# Revit family: Lighting_Pendants_Focus_Yoyo_Pendant
name_source: partatom
category: Lighting Fixtures
revit_build: Autodesk Revit 2017 (Build: 20190508_0315(x64)
units: mm (PartAtom-declared; Revit-internal decimal feet)

## family parameters
Always vertical = Yes
Cut with Voids When Loaded = No
Host = Ceiling
Light Source = Yes
OmniClass Number = 23.80.70.00
OmniClass Title = Lighting
Part Type = Normal
Room Calculation Point = No
Round Connector Dimension = Use Diameter
Shared = No

## types (1)
- Yoyo - Pendant
    AssetType = Fixed
    BIMObjectName = Lighting_Pendants_Focus_Yoyo_Pendant
    Brand = Focus Lighting
    Category = Indoor luminaires
    Color = Various
    Color Filter = 16777215
    Constituents = 3m white cable
    ConvergoRefNr = 0147-2006-0004-DK
    DefaultElevation = 0 mm  [stored 0 ft]
    Description = Yoyo is a new range of elegant indoor fixtures. The Yoyo luminaires are edge lit and are completely free of markings of internal components.
    Design = C.F. Møller Architects
    Dimming Lamp Color Temperature Shift = <None>
    DurationUnit = Hours
    ElectricalDeviceNominalPower = 0
    Emit Shape Visible in Rendering = No
    Emit from Circle Diameter = 610 mm
    ExpectedLife = 50000
    Features = LED: Edge lit; Top reflector + Light guide plate (LGP)
    Finish = Raw or painted aluminium
    HasProtectiveEarth = No
    IP_Code = IP20
    IfcExportAs = IfcLightFixtureType
    IfcExportType = NOTDEFINED
    InsulationStandardClass = Class 1
    LensMaterial = Acrylic, Clear
    LightFixtureMountingType = Suspended
    LightFixturePlacingType = Surface
    LightFixtureSecondaryMaterial = Plastic, Opaque White
    MaintenanceFactor = 0
    ManufacturerName = Focus Lighting
    ManufacturerURL = http://focus-lighting.dk
    Material = Aluminium
    NBSDescription = General purpose luminaires
    NBSReference = 90-60-50/405
    Name = Focus_Yoyo_Pendant
    NominalCurrent = 0 A
    NominalDiameter = 535 mm
    NominalFrequencyRange = 50 Hz
    NominalLength = 535 mm
    NominalRadius = 268 mm
    NominalVoltage = 220 V
    NominalVoltageCalc = 0 V
    NominalWidth = 535 mm
    NumberOfPoles = 1
    NumberOfSources = 0
    PhaseAngle = 0.00°
    Photometric Web File = YOYO 350 500mA 16W 3000K CRI90 CDP Prismatisk.IES
    ProductInformation = Yoyo is a new range of elegant indoor fixtures. The Yoyo luminaires are edge lit and are completely free of markings of internal components.
    Shape = Sculptured
    Size = 535x535x77 mm
    Tilt Angle = 90.00°
    TotalWattage = 26 W
    URL = https://focus-lighting.clients.ubivox.com
    Uniclass2 = Pr_70_70_49_86
    Uniclass2015Description = Pendant luminaires
    Uniclass2015Reference = Pr_70_70_48_62
    UsageCurrent = 0 A
    Version = 1
    VersionDate = 18/06/2020
    WarrantyDurationUnit = Hours
    Weight = 4.2 kg

note: [stored X ft] marks values corroborated as IEEE doubles in the binary element streams (Revit-internal decimal feet)

## geometry (parser evidence)
native form markers: Sweep x4
no freeform markers — native parametric forms only
